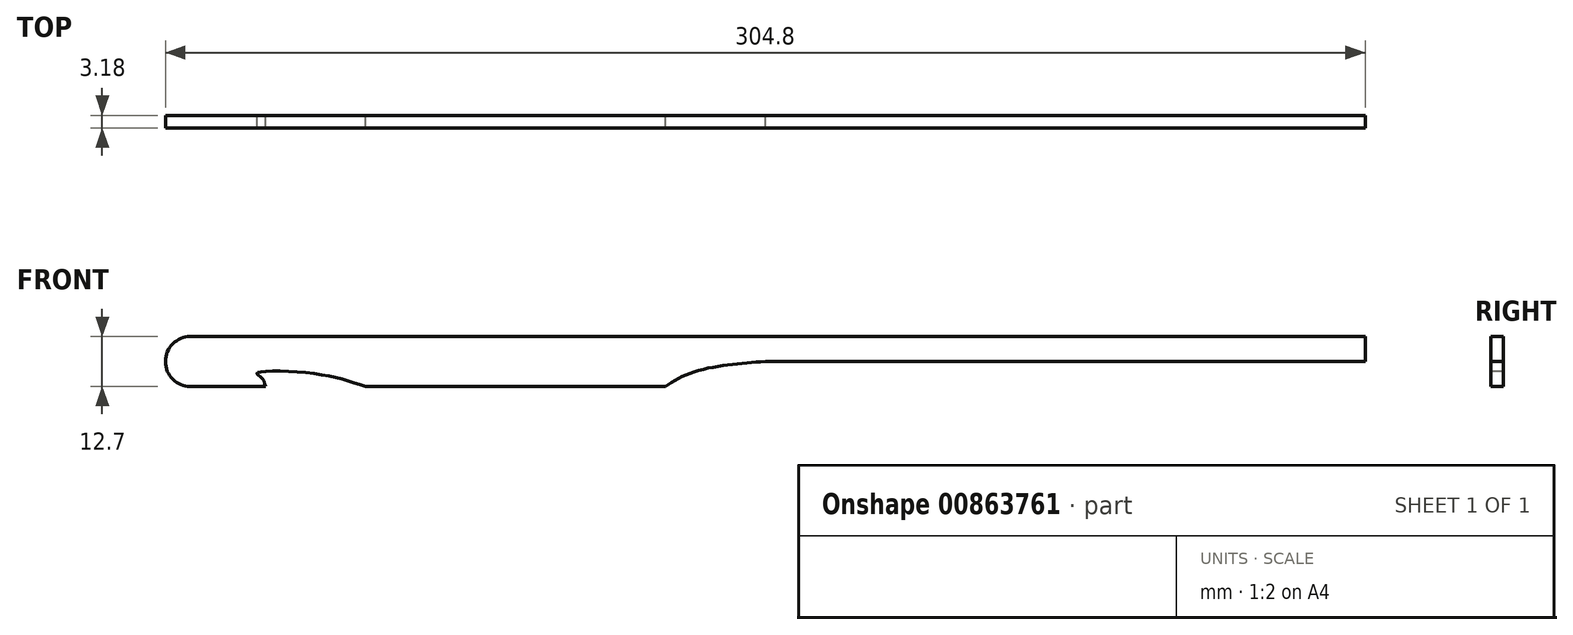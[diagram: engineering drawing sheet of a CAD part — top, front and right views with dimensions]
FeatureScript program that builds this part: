
annotation { "Feature Type Name" : "Feature", "Feature Type Description" : "" }
export const myFeature = defineFeature(function(context is Context, id is Id, definition is map)
    precondition{}
    {
        {
            var Q0;
            Q0=qCreatedBy(makeId("Front.planeOp"),FACE);
            var sketch = newSketch(context, id + "F0", { "sketchPlane" : qUnion([Q0])});
            skLineSegment(sketch, "E0.bottom", {"start": v(-124.05, -8.07) * mm, "end": v(-105, -8.07) * mm});
            skLineSegment(sketch, "E0.top", {"start": v(-124.05, 4.63) * mm, "end": v(174.4, 4.63) * mm});
            skLineSegment(sketch, "E0.right", {"start": v(174.4, -1.72) * mm, "end": v(174.4, 4.63) * mm});
            skPoint(sketch, "E1", {"position": v(-105, -8.07) * mm});
            skPoint(sketch, "E2", {"position": v(-79.6, -8.07) * mm});
            skFitSpline(sketch, "E3", {"points": [v(-105, -8.07) * mm, v(-105.93, -5.86) * mm, v(-107.13, -4.73) * mm, v(-93.62, -4.66) * mm, v(-79.6, -8.07) * mm], "startDerivative": vector(-3.34, 16.04) * mm, "endDerivative": vector(32.92, -11.08) * mm});
            skLineSegment(sketch, "E4.trimOffspring", {"start": v(-79.6, -8.07) * mm, "end": v(-3.4, -8.07) * mm});
            skPoint(sketch, "E5", {"position": v(22, -1.72) * mm});
            skPoint(sketch, "E6", {"position": v(-3.4, -8.07) * mm});
            skFitSpline(sketch, "E7", {"points": [v(-3.4, -8.07) * mm, v(2.64, -4.78) * mm, v(12.46, -2.6) * mm, v(22, -1.72) * mm], "startDerivative": vector(18.74, 12.16) * mm, "endDerivative": vector(26.85, 1.93) * mm});
            skLineSegment(sketch, "E8", {"start": v(174.4, -1.72) * mm, "end": v(22, -1.72) * mm});
            skPoint(sketch, "E9.orphan", {"position": v(174.4, -8.07) * mm});
            skPoint(sketch, "E10", {"position": v(-124.05, -8.07) * mm});
            skPoint(sketch, "E11.center.orphan", {"position": v(-130.4, -1.72) * mm});
            skArc(sketch, "E12", {"start": v(-124.05, 4.63) * mm, "mid": v(-130.4, -1.72) * mm, "end": v(-124.05, -8.07) * mm});
            skPoint(sketch, "E13.orphan", {"position": v(-130.4, 4.63) * mm});
            skPoint(sketch, "E14.orphan", {"position": v(-130.4, -8.07) * mm});
            skSolve(sketch);
        }
        {
            var Q0;
            Q0=makeQuery(id+"F0.imprint","IMPRINT",FACE,{"disambiguationData":[TD([[makeQuery(id+"F0.imprint","IMPRINT",EDGE,{"derivedFrom":sQuery(id+"F0.wireOp",EDGE,"E0.bottom")}),1.0]])]});
            extrude(context, id + "F1", {"entities" : qUnion([Q0]), "depth" : 3.17 * mm, "offsetDistance" : 25.4 * mm});
        }
    });
